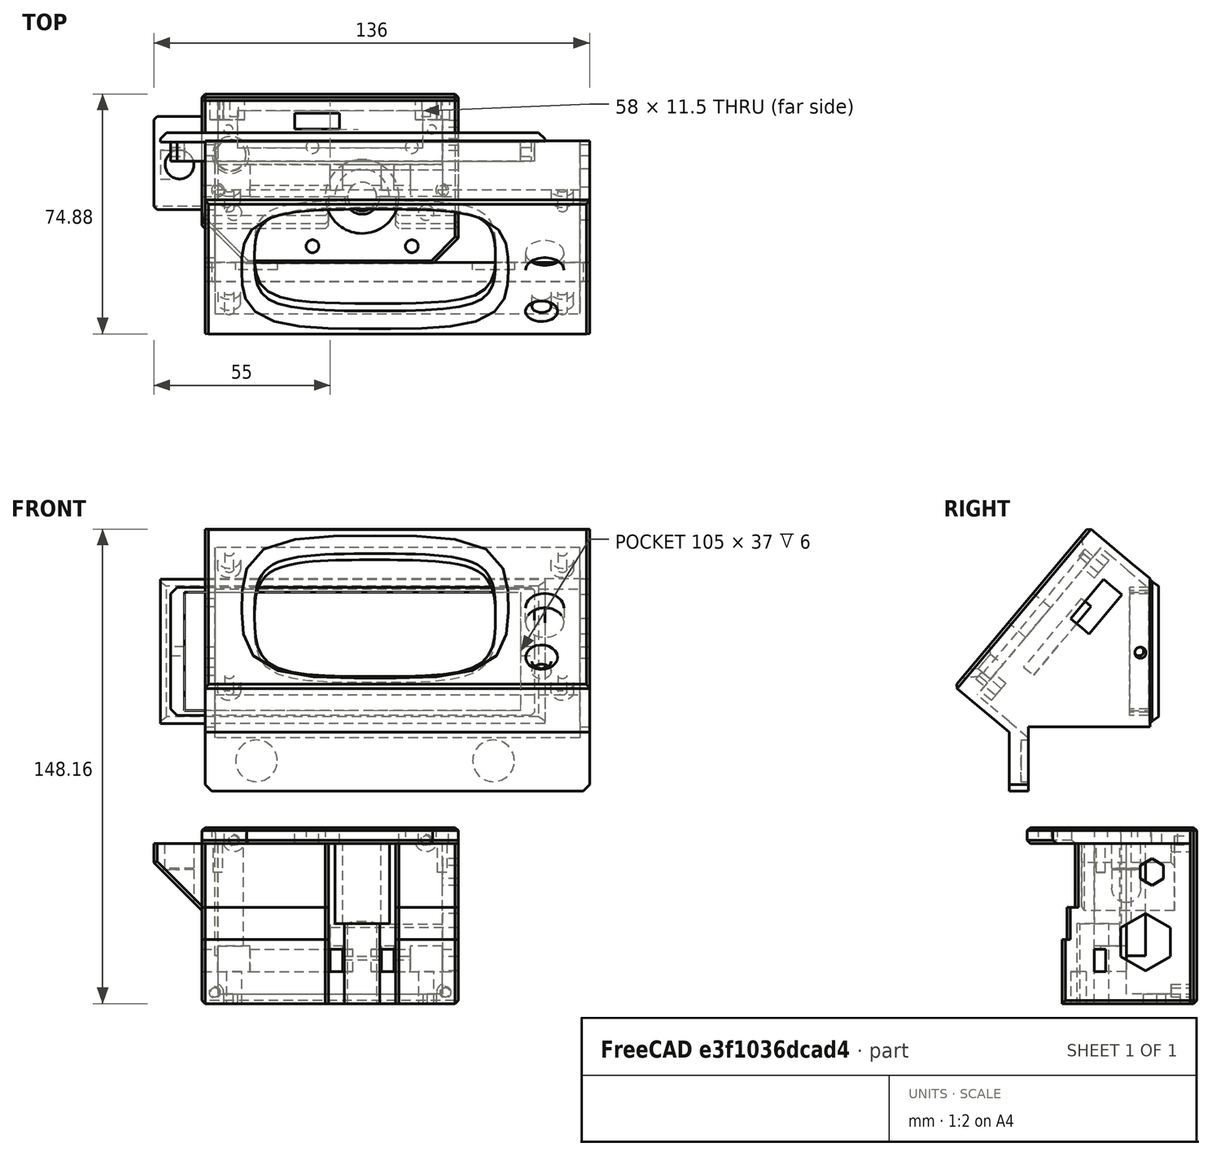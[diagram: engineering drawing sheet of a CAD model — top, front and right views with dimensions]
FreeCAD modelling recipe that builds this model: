
FCSTD DOCUMENT  (FreeCAD 0.19R)
Label: Ztower2
License: All rights reserved
LicenseURL: http://en.wikipedia.org/wiki/All_rights_reserved
objects: Sketcher::SketchObject×45, PartDesign::Pocket×31, PartDesign::Chamfer×18, PartDesign::Pad×13, PartDesign::Body×5, PartDesign::Mirrored×4, PartDesign::Fillet×1, Mesh::Feature×1
note: 180 computed .brp shape members not serialized (recipe doc carries the construction recipe); baked Part::Feature solids carry a one-line shape summary decoded from their .brp

FEATURE [Sketcher::SketchObject] Sketch  label="body"
  FullyConstrained = true
  MapMode = 5
  Support = -> [XY_Plane]
  sketch-geometry (6):
    g0: LineSegment StartX=-40 StartY=40 StartZ=0 EndX=40 EndY=40 EndZ=0
    g1: LineSegment StartX=40 StartY=40 StartZ=0 EndX=40 EndY=0 EndZ=0
    g2: LineSegment StartX=40 StartY=0 StartZ=0 EndX=-40 EndY=0 EndZ=0
    g3: LineSegment StartX=-40 StartY=0 StartZ=0 EndX=-40 EndY=40 EndZ=0
    g4: Circle CenterX=-30 CenterY=5 CenterZ=0 NormalX=0 NormalY=0 NormalZ=1 AngleXU=0 Radius=2.4
    g5: Circle CenterX=30 CenterY=5 CenterZ=0 NormalX=0 NormalY=0 NormalZ=1 AngleXU=0 Radius=2.4
  constraints (16):
    c: Coincident(g0,g1)
    c: Coincident(g1,g2)
    c: Coincident(g2,g3)
    c: Coincident(g3,g0)
    c: Horizontal(g0)
    c: Vertical(g1)
    c: Vertical(g3)
    c: PointOnObject(g1,g-1)
    c: Symmetric(g1,g2,g-2)
    c: Symmetric(g4,g5,g-2)
    c: Distance(g5,g4) = 60
    c: Diameter(g5) = 4.8
    c: Equal(g5,g4)
    c: DistanceY(g5) = 5
    c: Distance(g2) = 80
    c: Distance(g1) = 40
FEATURE [PartDesign::Pad] Pad
  Direction = (1,1,1)
  Length = 50
  Length2 = 100
  Profile = -> Sketch
  Type = 0
FEATURE [Sketcher::SketchObject] Sketch002  label="leadscrew"
  FullyConstrained = true
  MapMode = 5
  Placement = pos=(0,0,50) rot=(0,0,1;0rad)
  sketch-geometry (7):
    g0: Circle CenterX=10 CenterY=10 CenterZ=0 NormalX=0 NormalY=0 NormalZ=1 AngleXU=0 Radius=4.5
    g1: ArcOfCircle CenterX=10 CenterY=10 CenterZ=0 NormalX=0 NormalY=0 NormalZ=1 AngleXU=0 Radius=5.5 StartAngle=3.51376 EndAngle=5.91102
    g2: LineSegment StartX=4.87652 StartY=8 StartZ=0 EndX=0.876525 EndY=8 EndZ=0
    g3: LineSegment StartX=0.876525 StartY=8 StartZ=0 EndX=0.876525 EndY=-1.92 EndZ=0
    g4: LineSegment StartX=0.876525 StartY=-1.92 StartZ=0 EndX=19.1235 EndY=-1.92 EndZ=0
    g5: LineSegment StartX=19.1235 StartY=-1.92 StartZ=0 EndX=19.1235 EndY=8 EndZ=0
    g6: LineSegment StartX=15.1235 StartY=8 StartZ=0 EndX=19.1235 EndY=8 EndZ=0
  constraints (21):
    c: DistanceX(g0) = 10
    c: DistanceY(g0) = 10
    c: Diameter(g0) = 9
    c: Coincident(g1,g0)
    c: Coincident(g2,g1)
    c: Horizontal(g2)
    c: Coincident(g3,g2)
    c: Vertical(g3)
    c: Coincident(g4,g3)
    c: Horizontal(g4)
    c: Coincident(g5,g4)
    c: Vertical(g5)
    c: Coincident(g6,g1)
    c: Coincident(g6,g5)
    c: Horizontal(g6)
    c: DistanceY(g2) = 8
    c: DistanceY(g5) = 8
    c: Diameter(g1) = 11
    c: DistanceX(g2,g2) = 4
    c: Distance(g6) = 4
    c: DistanceY(g4) = -1.92
FEATURE [Sketcher::SketchObject] Sketch004  label="wiringbox"
  FullyConstrained = true
  MapMode = 5
  Placement = pos=(0,35,0) rot=(0,0.707107,0.707107;3.14159rad)
  sketch-geometry (4):
    g0: LineSegment StartX=-35 StartY=60 StartZ=0 EndX=35 EndY=60 EndZ=0
    g1: LineSegment StartX=35 StartY=60 StartZ=0 EndX=35 EndY=3 EndZ=0
    g2: LineSegment StartX=35 StartY=3 StartZ=0 EndX=-35 EndY=3 EndZ=0
    g3: LineSegment StartX=-35 StartY=3 StartZ=0 EndX=-35 EndY=60 EndZ=0
  constraints (11):
    c: Coincident(g0,g1)
    c: Coincident(g1,g2)
    c: Coincident(g2,g3)
    c: Coincident(g3,g0)
    c: Horizontal(g0)
    c: Vertical(g1)
    c: Vertical(g3)
    c: Symmetric(g1,g2,g-2)
    c: DistanceY(g1) = 3
    c: Distance(g2) = 70
    c: DistanceY(g0) = 60
FEATURE [Sketcher::SketchObject] Sketch005  label="DB37"
  FullyConstrained = false
  MapMode = 5
  Placement = pos=(0,1e-15,3) rot=(0,0,1;0rad)
  sketch-geometry (7):
    g0: LineSegment StartX=-29 StartY=36.75 StartZ=0 EndX=29 EndY=36.75 EndZ=0
    g1: LineSegment StartX=29 StartY=36.75 StartZ=0 EndX=29 EndY=25.25 EndZ=0
    g2: LineSegment StartX=29 StartY=25.25 StartZ=0 EndX=-29 EndY=25.25 EndZ=0
    g3: LineSegment StartX=-29 StartY=25.25 StartZ=0 EndX=-29 EndY=36.75 EndZ=0
    g4: Circle CenterX=-31.75 CenterY=31 CenterZ=0 NormalX=0 NormalY=0 NormalZ=1 AngleXU=0 Radius=1.4
    g5: Circle CenterX=31.75 CenterY=31 CenterZ=0 NormalX=0 NormalY=0 NormalZ=1 AngleXU=0 Radius=1.4
    g6: LineSegment StartX=-53.0593 StartY=31 StartZ=0 EndX=58.6364 EndY=31 EndZ=0
  constraints (17):
    c: Coincident(g0,g1)
    c: Coincident(g1,g2)
    c: Coincident(g2,g3)
    c: Coincident(g3,g0)
    c: Horizontal(g2)
    c: Vertical(g1)
    c: Vertical(g3)
    c: Distance(g0) = 58
    c: Symmetric(g0,g0,g-2)
    c: Distance(g1) = 11.5
    c: Distance(g5,g4) = 63.5
    c: Symmetric(g5,g4,g-2)
    c: Diameter(g5) = 2.8
    c: Equal(g5,g4)
    c: Symmetric(g2,g0,g6)
    c: PointOnObject(g4,g6)
    c: DistanceY(g6) = 31
FEATURE [Sketcher::SketchObject] Sketch006  label="sideports"
  FullyConstrained = true
  MapMode = 5
  Placement = pos=(-40,0,0) rot=(0.57735,-0.57735,-0.57735;2.0944rad)
  sketch-geometry (4):
    g0: LineSegment StartX=-13.5 StartY=17 StartZ=0 EndX=-10 EndY=17 EndZ=0
    g1: LineSegment StartX=-10 StartY=17 StartZ=0 EndX=-10 EndY=10 EndZ=0
    g2: LineSegment StartX=-10 StartY=10 StartZ=0 EndX=-13.5 EndY=10 EndZ=0
    g3: LineSegment StartX=-13.5 StartY=10 StartZ=0 EndX=-13.5 EndY=17 EndZ=0
  constraints (12):
    c: Coincident(g0,g1)
    c: Coincident(g1,g2)
    c: Coincident(g2,g3)
    c: Coincident(g3,g0)
    c: Horizontal(g0)
    c: Horizontal(g2)
    c: Vertical(g1)
    c: Vertical(g3)
    c: Distance(g2) = 3.5
    c: Distance(g3) = 7
    c: DistanceY(g1) = 10
    c: DistanceX(g1) = -10
FEATURE [Sketcher::SketchObject] Sketch007  label="ports"
  FullyConstrained = true
  MapMode = 5
  Placement = pos=(0,20,-5e-15) rot=(0,0.707107,0.707107;3.14159rad)
  sketch-geometry (8):
    g0: LineSegment StartX=-35 StartY=18 StartZ=0 EndX=-25 EndY=18 EndZ=0
    g1: LineSegment StartX=-25 StartY=18 StartZ=0 EndX=-25 EndY=10 EndZ=0
    g2: LineSegment StartX=-25 StartY=10 StartZ=0 EndX=-35 EndY=10 EndZ=0
    g3: LineSegment StartX=-35 StartY=10 StartZ=0 EndX=-35 EndY=18 EndZ=0
    g4: LineSegment StartX=25 StartY=18 StartZ=0 EndX=35 EndY=18 EndZ=0
    g5: LineSegment StartX=35 StartY=18 StartZ=0 EndX=35 EndY=10 EndZ=0
    g6: LineSegment StartX=35 StartY=10 StartZ=0 EndX=25 EndY=10 EndZ=0
    g7: LineSegment StartX=25 StartY=10 StartZ=0 EndX=25 EndY=18 EndZ=0
  constraints (23):
    c: Coincident(g0,g1)
    c: Coincident(g1,g2)
    c: Coincident(g2,g3)
    c: Coincident(g3,g0)
    c: Horizontal(g0)
    c: Horizontal(g2)
    c: Vertical(g1)
    c: Vertical(g3)
    c: Coincident(g4,g5)
    c: Coincident(g5,g6)
    c: Coincident(g6,g7)
    c: Coincident(g7,g4)
    c: Horizontal(g4)
    c: Horizontal(g6)
    c: Vertical(g5)
    c: Vertical(g7)
    c: DistanceY(g5) = 10
    c: DistanceY(g1) = 10
    c: Distance(g1) = 8
    c: Distance(g4) = 10
    c: Distance(g0) = 10
    c: Symmetric(g0,g4,g-2)
    c: DistanceX(g4) = 35
FEATURE [Sketcher::SketchObject] Sketch008  label="shtelfboss"
  FullyConstrained = true
  MapMode = 5
  Placement = pos=(0,35,0) rot=(0,0.707107,0.707107;3.14159rad)
  sketch-geometry (4):
    g0: LineSegment StartX=40 StartY=29 StartZ=0 EndX=55 EndY=44 EndZ=0
    g1: LineSegment StartX=55 StartY=44 StartZ=0 EndX=55 EndY=50 EndZ=0
    g2: LineSegment StartX=55 StartY=50 StartZ=0 EndX=40 EndY=50 EndZ=0
    g3: LineSegment StartX=40 StartY=50 StartZ=0 EndX=40 EndY=29 EndZ=0
  constraints (12):
    c: Coincident(g0,g1)
    c: Vertical(g1)
    c: Coincident(g1,g2)
    c: Horizontal(g2)
    c: Coincident(g2,g3)
    c: Coincident(g3,g0)
    c: Vertical(g3)
    c: DistanceX(g0) = 40
    c: Angle(g0) = 0.785398
    c: Distance(g1) = 6
    c: Distance(g2) = 15
    c: DistanceY(g2) = 50
FEATURE [Sketcher::SketchObject] Sketch009  label="umbillical"
  FullyConstrained = true
  MapMode = 5
  Placement = pos=(0,1.11e-14,50) rot=(0,0,1;0rad)
  sketch-geometry (8):
    g0: Circle CenterX=-47 CenterY=20 CenterZ=0 NormalX=0 NormalY=0 NormalZ=1 AngleXU=0 Radius=4.5
    g1: LineSegment StartX=-42.9 StartY=24.6329 StartZ=0 EndX=-42.9 EndY=29.3671 EndZ=0
    g2: LineSegment StartX=-42.9 StartY=29.3671 StartZ=0 EndX=-47 EndY=31.7343 EndZ=0
    g3: LineSegment StartX=-47 StartY=31.7343 StartZ=0 EndX=-51.1 EndY=29.3671 EndZ=0
    g4: LineSegment StartX=-51.1 StartY=29.3671 StartZ=0 EndX=-51.1 EndY=24.6329 EndZ=0
    g5: LineSegment StartX=-51.1 StartY=24.6329 StartZ=0 EndX=-47 EndY=22.2657 EndZ=0
    g6: LineSegment StartX=-47 StartY=22.2657 StartZ=0 EndX=-42.9 EndY=24.6329 EndZ=0
    g7: Circle CenterX=-47 CenterY=27 CenterZ=0 NormalX=0 NormalY=0 NormalZ=1 AngleXU=0 Radius=4.73427
  constraints (20):
    c: Diameter(g0) = 9
    c: DistanceX(g0) = -47
    c: Coincident(g1,g2)
    c: Coincident(g2,g3)
    c: Coincident(g3,g4)
    c: Coincident(g4,g5)
    c: Coincident(g5,g6)
    c: Coincident(g6,g1)
    c: Equal(g1, g2-g6) x5
    c: PointOnObject(g1,g7)
    c: PointOnObject(g2,g7)
    c: PointOnObject(g3,g7)
    c: PointOnObject(g4,g7)
    c: PointOnObject(g5,g7)
    c: PointOnObject(g6,g7)
    c: Distance(g4,g1) = 8.2
    c: DistanceX(g7) = -47
    c: Vertical(g4)
    c: DistanceY(g7) = 27
    c: DistanceY(g0) = 20
FEATURE [Sketcher::SketchObject] Sketch013  label="printhNotch"
  FullyConstrained = false
  MapMode = 5
  Placement = pos=(-52,0,0) rot=(0.57735,-0.57735,-0.57735;2.0944rad)
  sketch-geometry (4):
    g0: LineSegment StartX=-24.5 StartY=41.9 StartZ=0 EndX=-15.5 EndY=41.9 EndZ=0
    g1: LineSegment StartX=-15.5 StartY=41.9 StartZ=0 EndX=-15.5 EndY=36.1507 EndZ=0
    g2: LineSegment StartX=-15.5 StartY=36.1507 StartZ=0 EndX=-24.5 EndY=36.1507 EndZ=0
    g3: LineSegment StartX=-24.5 StartY=36.1507 StartZ=0 EndX=-24.5 EndY=41.9 EndZ=0
  constraints (11):
    c: Coincident(g0,g1)
    c: Coincident(g1,g2)
    c: Coincident(g2,g3)
    c: Coincident(g3,g0)
    c: Horizontal(g0)
    c: Horizontal(g2)
    c: Vertical(g1)
    c: Vertical(g3)
    c: Distance(g2) = 9
    c: DistanceX(g1) = -15.5
    c: DistanceY(g0) = 41.9
FEATURE [Sketcher::SketchObject] Sketch014  label="pritnfilm"
  FullyConstrained = false
  MapMode = 5
  Placement = pos=(0,0,41.9005) rot=(1,0,0;3.14159rad)
  sketch-geometry (4):
    g0: LineSegment StartX=-52.5605 StartY=-15.1127 StartZ=0 EndX=-40.6551 EndY=-15.1127 EndZ=0
    g1: LineSegment StartX=-40.6551 StartY=-15.1127 StartZ=0 EndX=-40.6551 EndY=-25.2911 EndZ=0
    g2: LineSegment StartX=-40.6551 StartY=-25.2911 StartZ=0 EndX=-52.5605 EndY=-25.2911 EndZ=0
    g3: LineSegment StartX=-52.5605 StartY=-25.2911 StartZ=0 EndX=-52.5605 EndY=-15.1127 EndZ=0
  constraints (8):
    c: Coincident(g0,g1)
    c: Coincident(g1,g2)
    c: Coincident(g2,g3)
    c: Coincident(g3,g0)
    c: Horizontal(g0)
    c: Horizontal(g2)
    c: Vertical(g1)
    c: Vertical(g3)
FEATURE [PartDesign::Pocket] Pocket
  BaseFeature = -> Pad
  Length = 5
  Length2 = 100
  Profile = -> Sketch002
  Type = 1
FEATURE [Sketcher::SketchObject] Sketch015  label="Coupler"
  FullyConstrained = true
  MapMode = 5
  Placement = pos=(0,0,50) rot=(0,0,1;0rad)
  Support = -> [Pocket]
  sketch-geometry (1):
    g0: Circle CenterX=10 CenterY=10 CenterZ=0 NormalX=0 NormalY=0 NormalZ=1 AngleXU=0 Radius=8.5
  constraints (3):
    c: DistanceX(g0) = 10
    c: DistanceY(g0) = 10
    c: Diameter(g0) = 17
FEATURE [PartDesign::Pocket] Pocket001
  BaseFeature = -> Pocket
  Length = 25
  Length2 = 100
  Profile = -> Sketch015
  Type = 0
FEATURE [PartDesign::Pocket] Pocket002
  BaseFeature = -> Pocket001
  Length = 15
  Length2 = 100
  Profile = -> Sketch004
  Type = 4
FEATURE [PartDesign::Pocket] Pocket003
  BaseFeature = -> Pocket002
  Length = 5
  Length2 = 100
  Profile = -> Sketch005
  Type = 0
FEATURE [PartDesign::Pocket] Pocket004
  BaseFeature = -> Pocket003
  Length = 5
  Length2 = 100
  Profile = -> Sketch006
  Type = 1
FEATURE [PartDesign::Pocket] Pocket005
  BaseFeature = -> Pocket004
  Length = 10
  Length2 = 100
  Profile = -> Sketch007
  Type = 0
FEATURE [PartDesign::Pad] Pad002
  BaseFeature = -> Pocket005
  Direction = (1,1,1)
  Length = 29
  Length2 = 100
  Profile = -> Sketch008
  Reversed = true
  Type = 0
FEATURE [PartDesign::Pocket] Pocket006
  BaseFeature = -> Pad002
  Length = 5
  Length2 = 100
  Profile = -> Sketch009
  Type = 1
FEATURE [PartDesign::Pocket] Pocket007
  BaseFeature = -> Pocket006
  Length = 5
  Length2 = 100
  Profile = -> Sketch013
  Type = 4
FEATURE [PartDesign::Pad] Pad003
  BaseFeature = -> Pocket007
  Direction = (1,1,1)
  Length = 0.3
  Length2 = 100
  Profile = -> Sketch014
  Reversed = true
  Type = 0
FEATURE [Sketcher::SketchObject] Sketch017  label="backReleif"
  FullyConstrained = true
  MapMode = 5
  Placement = pos=(40,0,0) rot=(0.57735,0.57735,0.57735;2.0944rad)
  sketch-geometry (6):
    g0: LineSegment StartX=4 StartY=53.2 StartZ=0 EndX=4 EndY=30 EndZ=0
    g1: LineSegment StartX=4 StartY=30 StartZ=0 EndX=1.5 EndY=30 EndZ=0
    g2: LineSegment StartX=-2.11 StartY=61.28 StartZ=0 EndX=4 EndY=53.2 EndZ=0
    g3: LineSegment StartX=1.5 StartY=30 StartZ=0 EndX=1.5 EndY=20 EndZ=0
    g4: LineSegment StartX=1.5 StartY=20 StartZ=0 EndX=-2.11 EndY=20 EndZ=0
    g5: LineSegment StartX=-2.11 StartY=20 StartZ=0 EndX=-2.11 EndY=61.28 EndZ=0
  constraints (18):
    c: Vertical(g0)
    c: Coincident(g0,g1)
    c: Coincident(g2,g0)
    c: DistanceX(g0) = 4
    c: DistanceY(g0) = 30
    c: Coincident(g1,g3)
    c: Vertical(g3)
    c: Coincident(g3,g4)
    c: Coincident(g4,g5)
    c: Vertical(g5)
    c: Coincident(g2,g5)
    c: Horizontal(g1)
    c: Horizontal(g4)
    c: DistanceY(g3) = 20
    c: DistanceX(g2) = -2.11
    c: DistanceY(g2) = 61.28
    c: DistanceY(g0) = 53.2
    c: DistanceX(g3) = 1.5
FEATURE [Sketcher::SketchObject] Sketch018  label="StepperPlatBolts"
  FullyConstrained = true
  MapMode = 5
  Placement = pos=(0,0,50) rot=(0,0,1;0rad)
  sketch-geometry (2):
    g0: Circle CenterX=-35 CenterY=12 CenterZ=0 NormalX=0 NormalY=0 NormalZ=1 AngleXU=0 Radius=1.4
    g1: Circle CenterX=35 CenterY=12 CenterZ=0 NormalX=0 NormalY=0 NormalZ=1 AngleXU=0 Radius=1.4
  constraints (5):
    c: Symmetric(g1,g0,g-2)
    c: Distance(g1,g0) = 70
    c: DistanceY(g1) = 12
    c: Diameter(g1) = 2.8
    c: Equal(g1,g0)
FEATURE [Sketcher::SketchObject] Sketch019  label="5mmbolts"
  FullyConstrained = true
  MapMode = 5
  Placement = pos=(0,0,0) rot=(1,0,0;3.14159rad)
  sketch-geometry (2):
    g0: Circle CenterX=-30 CenterY=-5 CenterZ=0 NormalX=0 NormalY=0 NormalZ=1 AngleXU=0 Radius=2.4
    g1: Circle CenterX=30 CenterY=-5 CenterZ=0 NormalX=0 NormalY=0 NormalZ=1 AngleXU=0 Radius=2.4
  constraints (5):
    c: Symmetric(g1,g0,g-2)
    c: Diameter(g1) = 4.8
    c: Equal(g1,g0)
    c: Distance(g1,g0) = 60
    c: DistanceY(g1) = -5
FEATURE [Sketcher::SketchObject] Sketch020  label="wirespace"
  FullyConstrained = true
  MapMode = 5
  Placement = pos=(0,0,0) rot=(1,0,0;3.14159rad)
  sketch-geometry (6):
    g0: ArcOfCircle CenterX=10 CenterY=-10 CenterZ=0 NormalX=0 NormalY=0 NormalZ=1 AngleXU=0 Radius=5.5 StartAngle=0 EndAngle=3.14159
    g1: LineSegment StartX=4.5 StartY=-10 StartZ=0 EndX=-0.5 EndY=-10 EndZ=0
    g2: LineSegment StartX=15.5 StartY=-10 StartZ=0 EndX=20.5 EndY=-10 EndZ=0
    g3: LineSegment StartX=20.5 StartY=-10 StartZ=0 EndX=20.5 EndY=2.44 EndZ=0
    g4: LineSegment StartX=-0.5 StartY=-10 StartZ=0 EndX=-0.5 EndY=2.44 EndZ=0
    g5: LineSegment StartX=-0.5 StartY=2.44 StartZ=0 EndX=20.5 EndY=2.44 EndZ=0
  constraints (19):
    c: Coincident(g1,g0)
    c: Horizontal(g1)
    c: Coincident(g2,g0)
    c: Horizontal(g2)
    c: Coincident(g3,g2)
    c: Vertical(g3)
    c: Coincident(g4,g1)
    c: Vertical(g4)
    c: Coincident(g5,g4)
    c: Coincident(g5,g3)
    c: Horizontal(g5)
    c: Distance(g2) = 5
    c: Distance(g1) = 5
    c: Diameter(g0) = 11
    c: DistanceY(g0) = -10
    c: DistanceY(g0) = -10
    c: DistanceX(g0) = 10
    c: DistanceY(g0) = -10
    c: DistanceY(g4) = 2.44
FEATURE [Sketcher::SketchObject] Sketch021  label="wirports"
  FullyConstrained = true
  MapMode = 5
  Placement = pos=(0,12,0) rot=(1,0,0;1.5708rad)
  sketch-geometry (8):
    g0: LineSegment StartX=16 StartY=18 StartZ=0 EndX=20 EndY=18 EndZ=0
    g1: LineSegment StartX=20 StartY=18 StartZ=0 EndX=20 EndY=10 EndZ=0
    g2: LineSegment StartX=20 StartY=10 StartZ=0 EndX=16 EndY=10 EndZ=0
    g3: LineSegment StartX=16 StartY=10 StartZ=0 EndX=16 EndY=18 EndZ=0
    g4: LineSegment StartX=0 StartY=18 StartZ=0 EndX=4 EndY=18 EndZ=0
    g5: LineSegment StartX=4 StartY=18 StartZ=0 EndX=4 EndY=10 EndZ=0
    g6: LineSegment StartX=4 StartY=10 StartZ=0 EndX=0 EndY=10 EndZ=0
    g7: LineSegment StartX=0 StartY=10 StartZ=0 EndX=0 EndY=18 EndZ=0
  constraints (24):
    c: Coincident(g0,g1)
    c: Coincident(g1,g2)
    c: Coincident(g2,g3)
    c: Coincident(g3,g0)
    c: Horizontal(g0)
    c: Horizontal(g2)
    c: Vertical(g1)
    c: Vertical(g3)
    c: Coincident(g4,g5)
    c: Coincident(g5,g6)
    c: Coincident(g6,g7)
    c: Coincident(g7,g4)
    c: Horizontal(g4)
    c: Horizontal(g6)
    c: Vertical(g5)
    c: Vertical(g7)
    c: PointOnObject(g4,g-2)
    c: DistanceY(g5) = 10
    c: DistanceY(g2) = 10
    c: DistanceY(g0) = 18
    c: DistanceY(g4) = 18
    c: DistanceX(g2) = 16
    c: DistanceX(g5) = 4
    c: DistanceX(g1) = 20
FEATURE [Sketcher::SketchObject] Sketch026  label="thickenerbump"
  FullyConstrained = false
  MapMode = 5
  Placement = pos=(0,0,50) rot=(0,0,1;0rad)
  sketch-geometry (4):
    g0: ArcOfCircle CenterX=9.88904 CenterY=9.80854 CenterZ=0 NormalX=0 NormalY=0 NormalZ=1 AngleXU=0 Radius=11.7902 StartAngle=0.279522 EndAngle=2.4698
    g1: ArcOfCircle CenterX=9.88904 CenterY=9.80854 CenterZ=0 NormalX=0 NormalY=0 NormalZ=1 AngleXU=0 Radius=9.47005 StartAngle=0.269167 EndAngle=2.60322
    g2: LineSegment StartX=1.75858 StartY=14.6642 StartZ=0 EndX=0.660759 EndY=17.1467 EndZ=0
    g3: LineSegment StartX=19.0181 StartY=12.3269 StartZ=0 EndX=21.2217 EndY=13.0614 EndZ=0
  constraints (5):
    c: Coincident(g1,g0)
    c: Coincident(g2,g1)
    c: Coincident(g2,g0)
    c: Coincident(g3,g1)
    c: Coincident(g3,g0)
FEATURE [Sketcher::SketchObject] Sketch003
  FullyConstrained = false
  MapMode = 5
  Support = -> [XY_Plane001]
  sketch-geometry (24):
    g0: LineSegment StartX=-11 StartY=31 StartZ=0 EndX=31 EndY=31 EndZ=0
    g1: LineSegment StartX=31 StartY=31 StartZ=0 EndX=31 EndY=-11 EndZ=0
    g2: LineSegment StartX=31 StartY=-11 StartZ=0 EndX=-11 EndY=-11 EndZ=0
    g3: LineSegment StartX=-11 StartY=-11 StartZ=0 EndX=-11 EndY=31 EndZ=0
    g4: Circle CenterX=10 CenterY=10 CenterZ=0 NormalX=0 NormalY=0 NormalZ=1 AngleXU=0 Radius=0.980681
    g5: LineSegment StartX=-40 StartY=40 StartZ=0 EndX=40 EndY=40 EndZ=0
    g6: LineSegment StartX=40 StartY=40 StartZ=0 EndX=40 EndY=-3 EndZ=0
    g7: LineSegment StartX=32 StartY=-11 StartZ=0 EndX=-26 EndY=-11 EndZ=0
    g8: LineSegment StartX=-40 StartY=3 StartZ=0 EndX=-40 EndY=40 EndZ=0
    g9: LineSegment StartX=-43.1827 StartY=10 StartZ=0 EndX=48.034 EndY=10 EndZ=0
    g10: Circle CenterX=10 CenterY=10 CenterZ=0 NormalX=0 NormalY=0 NormalZ=1 AngleXU=0 Radius=11.5
    g11: Circle CenterX=-35 CenterY=12 CenterZ=0 NormalX=0 NormalY=0 NormalZ=1 AngleXU=0 Radius=2
    g12: Circle CenterX=35 CenterY=12 CenterZ=0 NormalX=0 NormalY=0 NormalZ=1 AngleXU=0 Radius=2
    g13: LineSegment StartX=-11.0178 StartY=36.0399 StartZ=0 EndX=2.98222 EndY=36.0399 EndZ=0
    g14: LineSegment StartX=2.98222 StartY=36.0399 StartZ=0 EndX=2.98222 EndY=31.0399 EndZ=0
    g15: LineSegment StartX=2.98222 StartY=31.0399 StartZ=0 EndX=-11.0178 EndY=31.0399 EndZ=0
    g16: LineSegment StartX=-11.0178 StartY=31.0399 StartZ=0 EndX=-11.0178 EndY=36.0399 EndZ=0
    g17: Circle CenterX=25.5 CenterY=-5.5 CenterZ=0 NormalX=0 NormalY=0 NormalZ=1 AngleXU=0 Radius=2
    g18: Circle CenterX=-5.5 CenterY=25.5 CenterZ=0 NormalX=0 NormalY=0 NormalZ=1 AngleXU=0 Radius=2
    g19: Circle CenterX=-31 CenterY=23 CenterZ=0 NormalX=0 NormalY=0 NormalZ=1 AngleXU=0 Radius=4.75
    g20: Circle CenterX=25.5 CenterY=25.5 CenterZ=0 NormalX=0 NormalY=0 NormalZ=1 AngleXU=0 Radius=2
    g21: Circle CenterX=-5.5 CenterY=-5.5 CenterZ=0 NormalX=0 NormalY=0 NormalZ=1 AngleXU=0 Radius=2
    g22: LineSegment StartX=-40 StartY=3 StartZ=0 EndX=-26 EndY=-11 EndZ=0
    g23: LineSegment StartX=40 StartY=-3 StartZ=0 EndX=32 EndY=-11 EndZ=0
  constraints (62):
    c: Coincident(g0,g1)
    c: Coincident(g1,g2)
    c: Coincident(g2,g3)
    c: Coincident(g3,g0)
    c: Horizontal(g0)
    c: Horizontal(g2)
    c: Vertical(g1)
    c: Vertical(g3)
    c: Distance(g1) = 42
    c: Distance(g0) = 42
    c: Symmetric(g2,g0,g4)
    c: DistanceY(g4) = 10
    c: DistanceX(g4) = 10
    c: Coincident(g5,g6)
    c: Coincident(g8,g5)
    c: Horizontal(g5)
    c: Vertical(g6)
    c: Vertical(g8)
    c: DistanceY(g9) = 10
    c: Coincident(g10,g4)
    c: Diameter(g10) = 23
    c: DistanceY(g5) = 40
    c: Symmetric(g12,g11,g-2)
    c: Distance(g11,g12) = 70
    c: Diameter(g11) = 4
    c: Diameter(g12) = 4
    c: DistanceY(g12) = 12
    c: Coincident(g13,g14)
    c: Coincident(g14,g15)
    c: Coincident(g15,g16)
    c: Coincident(g16,g13)
    c: Horizontal(g13)
    c: Horizontal(g15)
    c: Vertical(g14)
    c: Vertical(g16)
    c: DistanceY(g10,g18) = 15.5
    c: DistanceX(g18,g10) = 15.5
    c: Diameter(g18) = 4
    c: Symmetric(g17,g18,g10)
    c: Diameter(g17) = 4
    c: Distance(g13) = 14
    c: Distance(g16) = 5
    c: DistanceX(g19) = -31
    c: DistanceY(g19) = 23
    c: Diameter(g19) = 9.5
    c: Symmetric(g20,g21,g10)
    c: Diameter(g20) = 4
    c: Equal(g20,g21)
    c: DistanceX(g10,g20) = 15.5
    c: DistanceY(g10,g20) = 15.5
    c: DistanceY(g8) = 3
    c: DistanceX(g5) = -40
    c: Coincident(g22,g8)
    c: Coincident(g7,g22)
    c: Angle(g22) = -0.785398
    c: DistanceX(g6) = 40
    c: Coincident(g23,g6)
    c: Coincident(g23,g7)
    c: Angle(g23) = -2.35619
    c: Horizontal(g7)
    c: DistanceY(g7) = -11
    c: DistanceY(g6) = -3
FEATURE [PartDesign::Pad] Pad001
  Direction = (1,1,1)
  Length = 5
  Length2 = 100
  Profile = -> Sketch003
  Type = 0
FEATURE [Sketcher::SketchObject] Sketch027
  FullyConstrained = true
  MapMode = 5
  Placement = pos=(0,0,13.5) rot=(1,0,0;3.14159rad)
  sketch-geometry (4):
    g0: LineSegment StartX=-50 StartY=30 StartZ=0 EndX=64 EndY=30 EndZ=0
    g1: LineSegment StartX=64 StartY=30 StartZ=0 EndX=64 EndY=-30 EndZ=0
    g2: LineSegment StartX=64 StartY=-30 StartZ=0 EndX=-50 EndY=-30 EndZ=0
    g3: LineSegment StartX=-50 StartY=-30 StartZ=0 EndX=-50 EndY=30 EndZ=0
  constraints (11):
    c: Coincident(g0,g1)
    c: Coincident(g1,g2)
    c: Coincident(g2,g3)
    c: Coincident(g3,g0)
    c: Horizontal(g0)
    c: Horizontal(g2)
    c: Vertical(g1)
    c: DistanceX(g0) = 64
    c: DistanceX(g0) = -50
    c: Distance(g3) = 60
    c: Symmetric(g2,g0,g-1)
FEATURE [Sketcher::SketchObject] Sketch028  label="knob"
  FullyConstrained = false
  MapMode = 5
  Placement = pos=(0,0,0) rot=(1,0,0;3.14159rad)
  sketch-geometry (1):
    g0: Circle CenterX=52 CenterY=20.5 CenterZ=0 NormalX=0 NormalY=0 NormalZ=1 AngleXU=0 Radius=3
  constraints (1):
    c: Diameter(g0) = 6
FEATURE [Sketcher::SketchObject] Sketch029
  FullyConstrained = true
  MapMode = 5
  Support = -> [XY_Plane002]
  sketch-geometry (30):
    g0: LineSegment StartX=-53 StartY=32.5 StartZ=0 EndX=67 EndY=32.5 EndZ=0
    g1: LineSegment StartX=67 StartY=32.5 StartZ=0 EndX=67 EndY=-32.5 EndZ=0
    g2: LineSegment StartX=67 StartY=-32.5 StartZ=0 EndX=-53 EndY=-32.5 EndZ=0
    g3: LineSegment StartX=-53 StartY=-32.5 StartZ=0 EndX=-53 EndY=32.5 EndZ=0
    g4: LineSegment StartX=-37 StartY=24.5 StartZ=0 EndX=37 EndY=24.5 EndZ=0
    g5: LineSegment StartX=37 StartY=24.5 StartZ=0 EndX=37 EndY=-24.5 EndZ=0
    g6: LineSegment StartX=37 StartY=-24.5 StartZ=0 EndX=-37 EndY=-24.5 EndZ=0
    g7: LineSegment StartX=-37 StartY=-24.5 StartZ=0 EndX=-37 EndY=24.5 EndZ=0
    g8: LineSegment StartX=-37.7408 StartY=25.116 StartZ=0 EndX=37.7408 EndY=25.116 EndZ=0
    g9: LineSegment StartX=37.7408 StartY=25.116 StartZ=0 EndX=37.7408 EndY=-25.116 EndZ=0
    g10: LineSegment StartX=37.7408 StartY=-25.116 StartZ=0 EndX=-37.7408 EndY=-25.116 EndZ=0
    g11: LineSegment StartX=-37.7408 StartY=-25.116 StartZ=0 EndX=-37.7408 EndY=25.116 EndZ=0
    g12-g19: Circle x8 (B-spline internal-alignment scaffolding for g20; pole/knot coordinates omitted)
    g20: BSplineCurve PolesCount=8 KnotsCount=9 Degree=3 IsPeriodic=1
    g21-g29: GeomPoint x9 (B-spline internal-alignment scaffolding for g20; pole/knot coordinates omitted)
  constraints (53):
    c: Coincident(g0,g1)
    c: Coincident(g1,g2)
    c: Coincident(g2,g3)
    c: Coincident(g3,g0)
    c: Horizontal(g0)
    c: Horizontal(g2)
    c: Vertical(g1)
    c: Vertical(g3)
    c: Coincident(g4,g5)
    c: Coincident(g5,g6)
    c: Coincident(g6,g7)
    c: Coincident(g7,g4)
    c: Horizontal(g4)
    c: Vertical(g7)
    c: Distance(g5) = 49
    c: Distance(g4,g3) = 16
    c: Distance(g0,g5) = 30
    c: Distance(g6,g2) = 8
    c: Distance(g4,g0) = 8
    c: Distance(g6) = 74
    c: Symmetric(g5,g6,g-2)
    c: Symmetric(g5,g4,g-1)
    c: Coincident(g8,g9)
    c: Coincident(g9,g10)
    c: Coincident(g10,g11)
    c: Coincident(g11,g8)
    c: Horizontal(g8)
    c: Horizontal(g10)
    c: Vertical(g9)
    c: Vertical(g11)
    c: Symmetric(g9,g8,g-1)
    c: Weight(g12) = 1
    c: Equal(g12,g13)
    c: Equal(g12,g14)
    c: Equal(g12,g15)
    c: PointOnObject(g15,g-1)
    c: Equal(g12,g16)
    c: Equal(g12,g17)
    c: PointOnObject(g17,g-2)
    c: Equal(g12,g18)
    c: Equal(g12,g19)
    c: InternalAlignment(g12-g19 -> g20) x8
    c: InternalAlignment(g21-g29 -> g20) x9
    c: Coincident(g8,g12)
    c: Coincident(g14,g8)
    c: Coincident(g16,g10)
    c: Coincident(g18,g9)
    c: Distance(g19,g5) = 0.5
    c: Symmetric(g19,g15,g-2)
    c: Distance(g17,g6) = 0.5
    c: Symmetric(g17,g13,g-1)
    c: DistanceX(g8) = 37.7408
    c: DistanceY(g8) = 25.116
FEATURE [PartDesign::Pad] Pad005
  Direction = (1,1,1)
  Length = 25
  Length2 = 100
  Profile = -> Sketch029
  Type = 0
FEATURE [PartDesign::Pocket] Pocket016
  BaseFeature = -> Pad005
  Length = 5
  Length2 = 100
  Profile = -> Sketch028
  Type = 1
FEATURE [Sketcher::SketchObject] Sketch001  label="knob001"
  FullyConstrained = false
  MapMode = 5
  Placement = pos=(0,0,25) rot=(0,0,1;0rad)
  Support = -> [Pocket016]
  sketch-geometry (1):
    g0: Circle CenterX=53 CenterY=-0.5 CenterZ=0 NormalX=0 NormalY=0 NormalZ=1 AngleXU=0 Radius=6
  constraints (2):
    c: Diameter(g0) = 12
    c: DistanceY(g0) = -0.5
FEATURE [PartDesign::Pocket] Pocket017
  BaseFeature = -> Pocket016
  Length = 5
  Length2 = 100
  Profile = -> Sketch001
  Type = 1
FEATURE [Sketcher::SketchObject] Sketch030
  FullyConstrained = true
  MapMode = 5
  Placement = pos=(0,0,0) rot=(1,0,0;3.14159rad)
  Support = -> [Pocket017]
  sketch-geometry (4):
    g0: LineSegment StartX=-50 StartY=30 StartZ=0 EndX=64 EndY=30 EndZ=0
    g1: LineSegment StartX=64 StartY=30 StartZ=0 EndX=64 EndY=-30 EndZ=0
    g2: LineSegment StartX=64 StartY=-30 StartZ=0 EndX=-50 EndY=-30 EndZ=0
    g3: LineSegment StartX=-50 StartY=-30 StartZ=0 EndX=-50 EndY=30 EndZ=0
  constraints (11):
    c: Coincident(g0,g1)
    c: Coincident(g1,g2)
    c: Coincident(g2,g3)
    c: Coincident(g3,g0)
    c: Horizontal(g0)
    c: Horizontal(g2)
    c: Vertical(g1)
    c: Symmetric(g2,g0,g-1)
    c: DistanceX(g0) = -50
    c: DistanceY(g0) = 30
    c: DistanceX(g1) = 64
FEATURE [PartDesign::Pocket] Pocket018
  BaseFeature = -> Pocket017
  Length = 18
  Length2 = 100
  Profile = -> Sketch030
  Type = 0
FEATURE [PartDesign::Chamfer] Chamfer001
  Angle = 45
  Base = -> Pocket018 [Edge19]
  BaseFeature = -> Pocket018
  ChamferType = 0
  FlipDirection = false
  Size = 4
  Size2 = 1
  SupportTransform = false
FEATURE [Sketcher::SketchObject] Sketch031  label="standofs"
  FullyConstrained = true
  MapMode = 5
  Placement = pos=(0,0,18) rot=(1,0,0;3.14159rad)
  Support = -> [Chamfer001]
  sketch-geometry (4):
    g0: Circle CenterX=-45.5 CenterY=25 CenterZ=0 NormalX=0 NormalY=0 NormalZ=1 AngleXU=0 Radius=3.5
    g1: Circle CenterX=-45.5 CenterY=-25 CenterZ=0 NormalX=0 NormalY=0 NormalZ=1 AngleXU=0 Radius=3.5
    g2: Circle CenterX=58.5 CenterY=-25 CenterZ=0 NormalX=0 NormalY=0 NormalZ=1 AngleXU=0 Radius=3.5
    g3: Circle CenterX=58.5 CenterY=25 CenterZ=0 NormalX=0 NormalY=0 NormalZ=1 AngleXU=0 Radius=3.5
  constraints (10):
    c: Diameter(g0) = 7
    c: Equal(g0,g1)
    c: Equal(g0,g3)
    c: Equal(g0,g2)
    c: Symmetric(g1,g0,g-1)
    c: Symmetric(g2,g3,g-1)
    c: Distance(g3,g2) = 50
    c: Distance(g1,g0) = 50
    c: Distance(g3,g0) = 104
    c: DistanceX(g0) = -45.5
FEATURE [PartDesign::Pad] Pad006
  BaseFeature = -> Chamfer001
  Direction = (1,1,1)
  Length = 4.5
  Length2 = 100
  Profile = -> Sketch031
  Type = 0
FEATURE [Sketcher::SketchObject] Sketch032  label="holes"
  FullyConstrained = true
  MapMode = 5
  Placement = pos=(0,0,13.5) rot=(1,0,0;3.14159rad)
  Support = -> [Pad006]
  sketch-geometry (4):
    g0: Circle CenterX=-45.5 CenterY=25 CenterZ=0 NormalX=0 NormalY=0 NormalZ=1 AngleXU=0 Radius=1.4
    g1: Circle CenterX=58.5 CenterY=25 CenterZ=0 NormalX=0 NormalY=0 NormalZ=1 AngleXU=0 Radius=1.4
    g2: Circle CenterX=58.5 CenterY=-25 CenterZ=0 NormalX=0 NormalY=0 NormalZ=1 AngleXU=0 Radius=1.4
    g3: Circle CenterX=-45.5 CenterY=-25 CenterZ=0 NormalX=0 NormalY=0 NormalZ=1 AngleXU=0 Radius=1.4
  constraints (10):
    c: Distance(g3,g2) = 104
    c: Distance(g3,g0) = 50
    c: Symmetric(g3,g0,g-1)
    c: Symmetric(g2,g1,g-1)
    c: Diameter(g1) = 2.8
    c: Equal(g1,g2)
    c: Equal(g1,g3)
    c: Equal(g1,g0)
    c: DistanceX(g0) = -45.5
    c: Distance(g1,g2) = 50
FEATURE [PartDesign::Pocket] Pocket019
  BaseFeature = -> Pad006
  Length = 8
  Length2 = 100
  Profile = -> Sketch032
  Type = 0
FEATURE [Sketcher::SketchObject] Sketch033
  ExternalGeometry = -> [Pocket019]
  FullyConstrained = true
  MapMode = 5
  Placement = pos=(67,0,0) rot=(0.57735,0.57735,0.57735;2.0944rad)
  Support = -> [Pocket019]
  sketch-geometry (4):
    g0: LineSegment StartX=7 StartY=6.5 StartZ=0 EndX=23 EndY=6.5 EndZ=0
    g1: LineSegment StartX=23 StartY=6.5 StartZ=0 EndX=23 EndY=0 EndZ=0
    g2: LineSegment StartX=23 StartY=0 StartZ=0 EndX=7 EndY=0 EndZ=0
    g3: LineSegment StartX=7 StartY=0 StartZ=0 EndX=7 EndY=6.5 EndZ=0
  constraints (12):
    c: Coincident(g0,g1)
    c: Coincident(g1,g2)
    c: Coincident(g2,g3)
    c: Coincident(g3,g0)
    c: Horizontal(g0)
    c: Horizontal(g2)
    c: Vertical(g1)
    c: Vertical(g3)
    c: Distance(g-3,g0) = 7
    c: Distance(g0) = 16
    c: Distance(g0,g-4) = 7
    c: PointOnObject(g1,g-1)
FEATURE [PartDesign::Pocket] Pocket020
  BaseFeature = -> Pocket019
  Length = 9
  Length2 = 100
  Profile = -> Sketch033
  Type = 0
FEATURE [Sketcher::SketchObject] Sketch034
  ExternalGeometry = -> [Pocket020]
  FullyConstrained = true
  MapMode = 5
  Placement = pos=(-53,0,0) rot=(0.57735,-0.57735,-0.57735;2.0944rad)
  Support = -> [Pocket020]
  sketch-geometry (4):
    g0: LineSegment StartX=-14 StartY=12.5 StartZ=0 EndX=14 EndY=12.5 EndZ=0
    g1: LineSegment StartX=14 StartY=12.5 StartZ=0 EndX=14 EndY=8.5 EndZ=0
    g2: LineSegment StartX=14 StartY=8.5 StartZ=0 EndX=-14 EndY=8.5 EndZ=0
    g3: LineSegment StartX=-14 StartY=8.5 StartZ=0 EndX=-14 EndY=12.5 EndZ=0
  constraints (11):
    c: Coincident(g0,g1)
    c: Coincident(g1,g2)
    c: Coincident(g2,g3)
    c: Coincident(g3,g0)
    c: Horizontal(g0)
    c: Vertical(g1)
    c: Vertical(g3)
    c: Distance(g0,g-3) = 1
    c: Distance(g1) = 4
    c: Symmetric(g1,g2,g-2)
    c: Distance(g2) = 28
FEATURE [PartDesign::Pocket] Pocket021
  BaseFeature = -> Pocket020
  Length = 5
  Length2 = 100
  Profile = -> Sketch034
  Type = 0
FEATURE [Sketcher::SketchObject] Sketch010
  FullyConstrained = false
  MapMode = 5
  Placement = pos=(-53,0,0) rot=(0.57735,-0.57735,-0.57735;2.0944rad)
  Support = -> [Pocket021]
  sketch-geometry (8):
    g0: LineSegment StartX=2.97644 StartY=-29.7683 StartZ=0 EndX=27.4024 EndY=-0.658582 EndZ=0
    g1: LineSegment StartX=27.4024 StartY=-0.658582 StartZ=0 EndX=42.7233 EndY=-13.5143 EndZ=0
    g2: LineSegment StartX=42.7233 StartY=-13.5143 StartZ=0 EndX=46.58 EndY=-8.91807 EndZ=0
    g3: LineSegment StartX=46.58 StartY=-8.91807 StartZ=0 EndX=27.4809 EndY=7.10801 EndZ=0
    g4: LineSegment StartX=-32.5 StartY=0 StartZ=0 EndX=2.97644 EndY=-29.7683 EndZ=0
    g5: LineSegment StartX=2.97644 StartY=-29.7683 StartZ=0 EndX=-60.5281 EndY=23.5183 EndZ=0
    g6: LineSegment StartX=27.4809 StartY=7.10801 StartZ=0 EndX=-32.5 EndY=7.10801 EndZ=0
    g7: LineSegment StartX=-32.5 StartY=7.10801 StartZ=0 EndX=-32.5 EndY=0 EndZ=0
  constraints (21):
    c: Coincident(g0,g1)
    c: Perpendicular(g1,g0)
    c: Coincident(g1,g2)
    c: Coincident(g2,g3)
    c: Coincident(g4,g0)
    c: Distance(g0) = 38
    c: Parallel(g1,g3)
    c: Perpendicular(g0,g4)
    c: Perpendicular(g1,g2)
    c: Distance(g2) = 6
    c: Angle(g0) = 0.872665
    c: Coincident(g5,g0)
    c: Perpendicular(g0,g5)
    c: PointOnObject(g4,g-1)
    c: Distance(g1) = 20
    c: Coincident(g6,g3)
    c: Horizontal(g6)
    c: DistanceX(g6) = -32.5
    c: Coincident(g7,g6)
    c: Vertical(g7)
    c: Coincident(g4,g7)
FEATURE [PartDesign::Pad] Pad007
  BaseFeature = -> Pocket021
  Direction = (1,1,1)
  Length = 120
  Length2 = 100
  Profile = -> Sketch010
  Reversed = true
  Type = 0
FEATURE [PartDesign::Pocket] Pocket022
  BaseFeature = -> Pad007
  Length = 47
  Length2 = 100
  Profile = -> Sketch027
  Reversed = true
  Type = 0
FEATURE [Sketcher::SketchObject] Sketch016
  FullyConstrained = true
  MapMode = 5
  Placement = pos=(67,0,0) rot=(0.57735,0.57735,0.57735;2.0944rad)
  Support = -> [Pocket022]
  sketch-geometry (4):
    g0: LineSegment StartX=7 StartY=11 StartZ=0 EndX=23 EndY=11 EndZ=0
    g1: LineSegment StartX=23 StartY=11 StartZ=0 EndX=23 EndY=3.5 EndZ=0
    g2: LineSegment StartX=23 StartY=3.5 StartZ=0 EndX=7 EndY=3.5 EndZ=0
    g3: LineSegment StartX=7 StartY=3.5 StartZ=0 EndX=7 EndY=11 EndZ=0
  constraints (12):
    c: Coincident(g0,g1)
    c: Coincident(g1,g2)
    c: Coincident(g2,g3)
    c: Coincident(g3,g0)
    c: Horizontal(g0)
    c: Horizontal(g2)
    c: Vertical(g1)
    c: Vertical(g3)
    c: Distance(g1) = 7.5
    c: Distance(g2) = 16
    c: DistanceX(g0) = 7
    c: DistanceY(g0) = 11
FEATURE [PartDesign::Pocket] Pocket023
  BaseFeature = -> Pocket022
  Length = 9
  Length2 = 100
  Profile = -> Sketch016
  Type = 0
FEATURE [PartDesign::Chamfer] Chamfer002
  Angle = 45
  Base = -> Pocket023 [Edge6]
  BaseFeature = -> Pocket023
  ChamferType = 0
  FlipDirection = false
  Size = 2
  Size2 = 1
  SupportTransform = false
FEATURE [Sketcher::SketchObject] Sketch022
  ExternalGeometry = -> [Chamfer002]
  FullyConstrained = true
  MapMode = 5
  Placement = pos=(-53,0,0) rot=(0.57735,-0.57735,-0.57735;2.0944rad)
  Support = -> [Chamfer002]
  sketch-geometry (2):
    g0: Circle CenterX=-12.8334 CenterY=-12.586 CenterZ=0 NormalX=0 NormalY=0 NormalZ=1 AngleXU=0 Radius=1.75
    g1: LineSegment StartX=-30.5716 StartY=2.29813 StartZ=0 EndX=4.90481 EndY=-27.4701 EndZ=0
  constraints (6):
    c: Parallel(g1,g-3)
    c: Distance(g1,g-3) = 3
    c: Equal(g1,g-3)
    c: Symmetric(g1,g1,g0)
    c: Diameter(g0) = 3.5
    c: PointOnObject(g1,g-4)
FEATURE [PartDesign::Pocket] Pocket024
  BaseFeature = -> Chamfer002
  Length = 5
  Length2 = 100
  Profile = -> Sketch022
  Type = 1
FEATURE [PartDesign::Chamfer] Chamfer005
  Angle = 45
  Base = -> Pocket024 [Edge97]
  BaseFeature = -> Pocket024
  ChamferType = 0
  FlipDirection = false
  Size = 2
  Size2 = 1
  SupportTransform = false
FEATURE [PartDesign::Chamfer] Chamfer006
  Angle = 45
  Base = -> Chamfer005 [Edge23]
  BaseFeature = -> Chamfer005
  ChamferType = 0
  FlipDirection = false
  Size = 2
  Size2 = 1
  SupportTransform = false
FEATURE [Sketcher::SketchObject] Sketch023
  FullyConstrained = true
  MapMode = 5
  Placement = pos=(0,-10.9977,13.1066) rot=(1,0,0;3.83972rad)
  Support = -> [Chamfer006]
  sketch-geometry (2):
    g0: Circle CenterX=-37 CenterY=32 CenterZ=0 NormalX=0 NormalY=0 NormalZ=1 AngleXU=0 Radius=6.5
    g1: Circle CenterX=37 CenterY=32 CenterZ=0 NormalX=0 NormalY=0 NormalZ=1 AngleXU=0 Radius=6.5
  constraints (5):
    c: Diameter(g1) = 13
    c: Equal(g1,g0)
    c: Symmetric(g1,g0,g-2)
    c: DistanceY(g0) = 32
    c: Distance(g1,g0) = 74
FEATURE [PartDesign::Pocket] Pocket025
  BaseFeature = -> Chamfer006
  Length = 2.3
  Length2 = 100
  Profile = -> Sketch023
  Type = 0
FEATURE [PartDesign::Chamfer] Chamfer007
  Angle = 45
  Base = -> Pocket025 [Edge74,Edge75,Edge31,Edge67]
  BaseFeature = -> Pocket025
  ChamferType = 0
  FlipDirection = false
  Size = 1
  Size2 = 1
  SupportTransform = false
FEATURE [Sketcher::SketchObject] Sketch035
  ExternalGeometry = -> [Chamfer002]
  FullyConstrained = false
  MapMode = 5
  Placement = pos=(0,13.4282,-16.0031) rot=(1,0,0;3.83972rad)
  Support = -> [Chamfer002]
  sketch-geometry (4):
    g0: LineSegment StartX=-53 StartY=-24.6078 StartZ=0 EndX=67 EndY=-24.6078 EndZ=0
    g1: LineSegment StartX=67 StartY=-24.6078 StartZ=0 EndX=67 EndY=20.3922 EndZ=0
    g2: LineSegment StartX=67 StartY=20.3922 StartZ=0 EndX=-53 EndY=20.3922 EndZ=0
    g3: LineSegment StartX=-53 StartY=20.3922 StartZ=0 EndX=-53 EndY=-24.6078 EndZ=0
  constraints (11):
    c: Coincident(g0,g1)
    c: Coincident(g1,g2)
    c: Coincident(g2,g3)
    c: Coincident(g3,g0)
    c: Horizontal(g0)
    c: Horizontal(g2)
    c: Vertical(g1)
    c: Vertical(g3)
    c: Distance(g2) = 120
    c: DistanceX(g2) = -53
    c: Distance(g3) = 45
FEATURE [PartDesign::Body] Body002  label="ScreenBox"
  Group = -> [Sketch029,Pad005,Sketch001,Sketch028,Pocket016,Pocket017,Sketch030,Pocket018,Chamfer001,Sketch031,Pad006,Sketch032,Pocket019,Sketch033,Pocket020,Sketch034,Pocket021,Sketch010,Pad007,Sketch027,Pocket022,Sketch016,Pocket023,Chamfer002,Sketch035,Sketch022,Pocket024,Chamfer005,Chamfer006,Sketch023,Pocket025,Chamfer007]
  Origin = -> Origin002
  Placement = pos=(14,6.52211,107.834) rot=(1,0,0;0.872665rad)
  Tip = -> Chamfer007
FEATURE [Sketcher::SketchObject] Sketch036
  FullyConstrained = true
  MapMode = 5
  Placement = pos=(0,-9,1.5e-14) rot=(1,0,0;1.5708rad)
  sketch-geometry (4):
    g0: LineSegment StartX=-52.5 StartY=18.5 StartZ=0 EndX=52.5 EndY=18.5 EndZ=0
    g1: LineSegment StartX=52.5 StartY=18.5 StartZ=0 EndX=52.5 EndY=-18.5 EndZ=0
    g2: LineSegment StartX=52.5 StartY=-18.5 StartZ=0 EndX=-52.5 EndY=-18.5 EndZ=0
    g3: LineSegment StartX=-52.5 StartY=-18.5 StartZ=0 EndX=-52.5 EndY=18.5 EndZ=0
  constraints (11):
    c: Coincident(g0,g1)
    c: Coincident(g1,g2)
    c: Coincident(g2,g3)
    c: Coincident(g3,g0)
    c: Horizontal(g0)
    c: Horizontal(g2)
    c: Vertical(g1)
    c: Vertical(g3)
    c: Distance(g0) = 105
    c: Symmetric(g0,g2,g-1)
    c: Distance(g1) = 37
FEATURE [Sketcher::SketchObject] Sketch037
  FullyConstrained = true
  MapMode = 5
  Placement = pos=(0,0,0) rot=(1,0,0;1.5708rad)
  Support = -> [XZ_Plane003]
  sketch-geometry (4):
    g0: LineSegment StartX=-60 StartY=22.5 StartZ=0 EndX=60 EndY=22.5 EndZ=0
    g1: LineSegment StartX=60 StartY=22.5 StartZ=0 EndX=60 EndY=-22.5 EndZ=0
    g2: LineSegment StartX=60 StartY=-22.5 StartZ=0 EndX=-60 EndY=-22.5 EndZ=0
    g3: LineSegment StartX=-60 StartY=-22.5 StartZ=0 EndX=-60 EndY=22.5 EndZ=0
  constraints (10):
    c: Coincident(g0,g1)
    c: Coincident(g1,g2)
    c: Coincident(g2,g3)
    c: Coincident(g3,g0)
    c: Horizontal(g2)
    c: Vertical(g3)
    c: Symmetric(g0,g0,g-2)
    c: Distance(g0) = 120
    c: Distance(g1) = 45
    c: Symmetric(g1,g0,g-1)
FEATURE [PartDesign::Pad] Pad008
  Direction = (1,1,1)
  Length = 3
  Length2 = 100
  Placement = pos=(0,0,0) rot=(1,0,0;1.5708rad)
  Profile = -> Sketch037
  Type = 0
FEATURE [Sketcher::SketchObject] Sketch038
  FullyConstrained = true
  MapMode = 5
  Placement = pos=(0,-3,7e-16) rot=(1,0,0;1.5708rad)
  Support = -> [Pad008]
  sketch-geometry (4):
    g0: LineSegment StartX=-56.75 StartY=20 StartZ=0 EndX=56.75 EndY=20 EndZ=0
    g1: LineSegment StartX=56.75 StartY=20 StartZ=0 EndX=56.75 EndY=-20 EndZ=0
    g2: LineSegment StartX=56.75 StartY=-20 StartZ=0 EndX=-56.75 EndY=-20 EndZ=0
    g3: LineSegment StartX=-56.75 StartY=-20 StartZ=0 EndX=-56.75 EndY=20 EndZ=0
  constraints (11):
    c: Coincident(g0,g1)
    c: Coincident(g1,g2)
    c: Coincident(g2,g3)
    c: Coincident(g3,g0)
    c: Horizontal(g0)
    c: Horizontal(g2)
    c: Vertical(g1)
    c: Vertical(g3)
    c: Distance(g0) = 113.5
    c: Distance(g1) = 40
    c: Symmetric(g1,g0,g-1)
FEATURE [PartDesign::Pad] Pad009
  BaseFeature = -> Pad008
  Direction = (1,1,1)
  Length = 6
  Length2 = 100
  Placement = pos=(0,0,0) rot=(1,0,0;1.5708rad)
  Profile = -> Sketch038
  Type = 0
FEATURE [Sketcher::SketchObject] Sketch039
  FullyConstrained = true
  MapMode = 5
  Placement = pos=(56.75,0,0) rot=(0.707107,0,0.707107;3.14159rad)
  Support = -> [Pad009]
  sketch-geometry (1):
    g0: Circle CenterX=0 CenterY=6 CenterZ=0 NormalX=0 NormalY=0 NormalZ=1 AngleXU=0 Radius=1.4
  constraints (3):
    c: PointOnObject(g0,g-2)
    c: Diameter(g0) = 2.8
    c: DistanceY(g0) = 6
FEATURE [PartDesign::Pocket] Pocket026
  BaseFeature = -> Pad009
  Length = 5
  Length2 = 100
  Placement = pos=(0,0,0) rot=(1,0,0;1.5708rad)
  Profile = -> Sketch039
  Type = 1
FEATURE [Sketcher::SketchObject] Sketch040
  ExternalGeometry = -> [Pocket026]
  FullyConstrained = false
  MapMode = 5
  Placement = pos=(60,0,0) rot=(0.707107,0,0.707107;3.14159rad)
  Support = -> [Pocket026]
  sketch-geometry (3):
    g0: LineSegment StartX=-22.5 StartY=3 StartZ=0 EndX=-17.8755 EndY=-3.60453 EndZ=0
    g1: LineSegment StartX=-17.8755 StartY=-3.60453 StartZ=0 EndX=-35.5163 EndY=-3.60453 EndZ=0
    g2: LineSegment StartX=-35.5163 StartY=-3.60453 StartZ=0 EndX=-22.5 EndY=3 EndZ=0
  constraints (6):
    c: Coincident(g0,g1)
    c: Horizontal(g1)
    c: Coincident(g1,g2)
    c: Coincident(g2,g0)
    c: Angle(g0) = -0.959931
    c: Coincident(g0,g-3)
FEATURE [PartDesign::Pocket] Pocket027
  BaseFeature = -> Pocket026
  Length = 5
  Length2 = 100
  Placement = pos=(0,0,0) rot=(1,0,0;1.5708rad)
  Profile = -> Sketch040
  Type = 1
FEATURE [PartDesign::Mirrored] Mirrored
  BaseFeature = -> Pocket027
  MirrorPlane = -> Sketch040 [V_Axis]
  Originals = -> [Pocket027]
  Placement = pos=(0,0,0) rot=(1,0,0;1.5708rad)
FEATURE [PartDesign::Chamfer] Chamfer008
  Angle = 45
  Base = -> Mirrored [Edge14,Edge12]
  BaseFeature = -> Mirrored
  ChamferType = 0
  FlipDirection = false
  Placement = pos=(0,0,0) rot=(1,0,0;1.5708rad)
  Size = 2
  Size2 = 1
  SupportTransform = false
FEATURE [PartDesign::Pocket] Pocket028
  BaseFeature = -> Chamfer008
  Length = 6
  Length2 = 100
  Placement = pos=(0,0,0) rot=(1,0,0;1.5708rad)
  Profile = -> Sketch036
  Type = 0
FEATURE [PartDesign::Chamfer] Chamfer009
  Angle = 45
  Base = -> Pocket028 [Edge29]
  BaseFeature = -> Pocket028
  ChamferType = 0
  FlipDirection = false
  Placement = pos=(0,0,0) rot=(1,0,0;1.5708rad)
  Size = 2
  Size2 = 1
  SupportTransform = false
FEATURE [PartDesign::Chamfer] Chamfer010
  Angle = 45
  Base = -> Chamfer009 [Edge11]
  BaseFeature = -> Chamfer009
  ChamferType = 0
  FlipDirection = false
  Placement = pos=(0,0,0) rot=(1,0,0;1.5708rad)
  Size = 1
  Size2 = 1
  SupportTransform = false
FEATURE [PartDesign::Chamfer] Chamfer011
  Angle = 45
  Base = -> Chamfer010 [Edge18]
  BaseFeature = -> Chamfer010
  ChamferType = 0
  FlipDirection = false
  Placement = pos=(0,0,0) rot=(1,0,0;1.5708rad)
  Size = 1
  Size2 = 1
  SupportTransform = false
FEATURE [PartDesign::Chamfer] Chamfer012
  Angle = 45
  Base = -> Chamfer011 [Edge20]
  BaseFeature = -> Chamfer011
  ChamferType = 0
  FlipDirection = false
  Placement = pos=(0,0,0) rot=(1,0,0;1.5708rad)
  Size = 2
  Size2 = 1
  SupportTransform = false
FEATURE [PartDesign::Body] Body003  label="BoxCap"
  Group = -> [Sketch037,Pad008,Sketch038,Pad009,Sketch039,Pocket026,Sketch036,Sketch040,Pocket027,Mirrored,Chamfer008,Pocket028,Chamfer009,Chamfer010,Chamfer011,Chamfer012]
  Origin = -> Origin003
  Placement = pos=(7,30,110) rot=(0,0,1;0rad)
  Tip = -> Chamfer012
FEATURE [Sketcher::SketchObject] Sketch042  label="buttonHoles"
  FullyConstrained = false
  MapMode = 5
  Placement = pos=(40,0,0) rot=(0.57735,0.57735,0.57735;2.0944rad)
  sketch-geometry (14):
    g0: LineSegment StartX=26 StartY=10.1945 StartZ=0 EndX=33.8 EndY=14.6979 EndZ=0
    g1: LineSegment StartX=33.8 StartY=14.6979 StartZ=0 EndX=33.8 EndY=23.7045 EndZ=0
    g2: LineSegment StartX=33.8 StartY=23.7045 StartZ=0 EndX=26 EndY=28.2079 EndZ=0
    g3: LineSegment StartX=26 StartY=28.2079 StartZ=0 EndX=18.2 EndY=23.7045 EndZ=0
    g4: LineSegment StartX=18.2 StartY=23.7045 StartZ=0 EndX=18.2 EndY=14.6979 EndZ=0
    g5: LineSegment StartX=18.2 StartY=14.6979 StartZ=0 EndX=26 EndY=10.1945 EndZ=0
    g6: Circle CenterX=26 CenterY=19.2012 CenterZ=0 NormalX=0 NormalY=0 NormalZ=1 AngleXU=0 Radius=9.00666
    g7: LineSegment StartX=31.6 StartY=39.0374 StartZ=0 EndX=31.6 EndY=43.1943 EndZ=0
    g8: LineSegment StartX=31.6 StartY=43.1943 StartZ=0 EndX=28 EndY=45.2728 EndZ=0
    g9: LineSegment StartX=28 StartY=45.2728 StartZ=0 EndX=24.4 EndY=43.1943 EndZ=0
    g10: LineSegment StartX=24.4 StartY=43.1943 StartZ=0 EndX=24.4 EndY=39.0374 EndZ=0
    g11: LineSegment StartX=24.4 StartY=39.0374 StartZ=0 EndX=28 EndY=36.959 EndZ=0
    g12: LineSegment StartX=28 StartY=36.959 StartZ=0 EndX=31.6 EndY=39.0374 EndZ=0
    g13: Circle CenterX=28 CenterY=41.1159 CenterZ=0 NormalX=0 NormalY=0 NormalZ=1 AngleXU=0 Radius=4.15692
  constraints (32):
    c: Coincident(g0,g1)
    c: Coincident(g1,g2)
    c: Coincident(g2,g3)
    c: Coincident(g3,g4)
    c: Coincident(g4,g5)
    c: Coincident(g5,g0)
    c: Equal(g0, g1-g5) x5
    c: PointOnObject(g0,g6)
    c: PointOnObject(g1,g6)
    c: PointOnObject(g2,g6)
    c: PointOnObject(g3,g6)
    c: PointOnObject(g4,g6)
    c: PointOnObject(g5,g6)
    c: Coincident(g7,g8)
    c: Coincident(g8,g9)
    c: Coincident(g9,g10)
    c: Coincident(g10,g11)
    c: Coincident(g11,g12)
    c: Coincident(g12,g7)
    c: Equal(g7, g8-g12) x5
    c: PointOnObject(g7,g13)
    c: PointOnObject(g8,g13)
    c: PointOnObject(g9,g13)
    c: PointOnObject(g10,g13)
    c: PointOnObject(g11,g13)
    c: PointOnObject(g12,g13)
    c: Distance(g0,g4) = 15.6
    c: Vertical(g1)
    c: Vertical(g7)
    c: Distance(g7,g10) = 7.2
    c: DistanceX(g6) = 26
    c: DistanceX(g13) = 28
FEATURE [Sketcher::SketchObject] Sketch044  label="umbchannel"
  FullyConstrained = true
  MapMode = 5
  Placement = pos=(0,0,50) rot=(0,0,1;0rad)
  sketch-geometry (1):
    g0: Circle CenterX=-31 CenterY=23 CenterZ=0 NormalX=0 NormalY=0 NormalZ=1 AngleXU=0 Radius=5
  constraints (3):
    c: Diameter(g0) = 10
    c: DistanceX(g0) = -31
    c: DistanceY(g0) = 23
FEATURE [PartDesign::Pocket] Pocket029
  BaseFeature = -> Pad003
  Length = 5
  Length2 = 100
  Profile = -> Sketch017
  Type = 1
FEATURE [PartDesign::Pocket] Pocket030
  BaseFeature = -> Pocket029
  Length = 9
  Length2 = 100
  Profile = -> Sketch018
  Type = 0
FEATURE [PartDesign::Pocket] Pocket031
  BaseFeature = -> Pocket030
  Length = 10
  Length2 = 100
  Profile = -> Sketch019
  Type = 0
FEATURE [PartDesign::Pocket] Pocket032
  BaseFeature = -> Pocket031
  Length = 5
  Length2 = 100
  Profile = -> Sketch020
  Type = 1
FEATURE [PartDesign::Pocket] Pocket033
  BaseFeature = -> Pocket032
  Length = 5
  Length2 = 100
  Profile = -> Sketch021
  Type = 1
FEATURE [Sketcher::SketchObject] Sketch025  label="CoverBolts"
  FullyConstrained = true
  MapMode = 5
  Placement = pos=(0,40,0) rot=(0,0.707107,0.707107;3.14159rad)
  Support = -> [Pocket033]
  sketch-geometry (1):
    g0: Circle CenterX=-36 CenterY=3.5 CenterZ=0 NormalX=0 NormalY=0 NormalZ=1 AngleXU=0 Radius=2.75
  constraints (3):
    c: Diameter(g0) = 5.5
    c: DistanceY(g0) = 3.5
    c: DistanceX(g0) = -36
FEATURE [Sketcher::SketchObject] Sketch045
  FullyConstrained = true
  MapMode = 5
  Placement = pos=(0,0,0) rot=(1,0,0;1.5708rad)
  Support = -> [XZ_Plane004]
  sketch-geometry (4):
    g0: LineSegment StartX=-40 StartY=55 StartZ=0 EndX=40 EndY=55 EndZ=0
    g1: LineSegment StartX=40 StartY=55 StartZ=0 EndX=40 EndY=0 EndZ=0
    g2: LineSegment StartX=40 StartY=0 StartZ=0 EndX=-40 EndY=0 EndZ=0
    g3: LineSegment StartX=-40 StartY=0 StartZ=0 EndX=-40 EndY=55 EndZ=0
  constraints (11):
    c: Coincident(g0,g1)
    c: Coincident(g1,g2)
    c: Coincident(g2,g3)
    c: Coincident(g3,g0)
    c: Horizontal(g2)
    c: Vertical(g1)
    c: Vertical(g3)
    c: Distance(g1) = 55
    c: Distance(g0) = 80
    c: Symmetric(g0,g0,g-2)
    c: PointOnObject(g1,g-1)
FEATURE [PartDesign::Pad] Pad012
  Direction = (1,1,1)
  Length = 2
  Length2 = 100
  Placement = pos=(0,0,0) rot=(1,0,0;1.5708rad)
  Profile = -> Sketch045
  Type = 0
FEATURE [Sketcher::SketchObject] Sketch046
  FullyConstrained = true
  MapMode = 5
  Placement = pos=(0,0,0) rot=(-1,0,0;1.5708rad)
  Support = -> [Pad012]
  sketch-geometry (2):
    g0: Circle CenterX=-36 CenterY=-3.5 CenterZ=0 NormalX=0 NormalY=0 NormalZ=1 AngleXU=0 Radius=1.75
    g1: Circle CenterX=-30 CenterY=-51 CenterZ=0 NormalX=0 NormalY=0 NormalZ=1 AngleXU=0 Radius=1.75
  constraints (6):
    c: DistanceY(g1) = -51
    c: Diameter(g1) = 3.5
    c: Equal(g1,g0)
    c: DistanceX(g0) = -36
    c: DistanceX(g1) = -30
    c: DistanceY(g0) = -3.5
FEATURE [PartDesign::Pocket] Pocket037
  BaseFeature = -> Pad012
  Length = 5
  Length2 = 100
  Placement = pos=(0,0,0) rot=(1,0,0;1.5708rad)
  Profile = -> Sketch046
  Type = 0
FEATURE [PartDesign::Mirrored] Mirrored001
  BaseFeature = -> Pocket037
  MirrorPlane = -> Sketch046 [V_Axis]
  Originals = -> [Pocket037]
  Placement = pos=(0,0,0) rot=(1,0,0;1.5708rad)
FEATURE [PartDesign::Chamfer] Chamfer
  Angle = 45
  Base = -> Mirrored001 [Edge9,Edge3,Edge11,Edge6,Edge2,Edge1,Edge5,Edge8]
  BaseFeature = -> Mirrored001
  ChamferType = 0
  FlipDirection = false
  Placement = pos=(0,0,0) rot=(1,0,0;1.5708rad)
  Size = 1
  Size2 = 1
  SupportTransform = false
FEATURE [PartDesign::Body] Body004  label="Cover"
  Group = -> [Sketch045,Pad012,Sketch046,Pocket037,Mirrored001,Chamfer]
  Origin = -> Origin004
  Placement = pos=(0,42,0) rot=(0,0,1;0rad)
  Tip = -> Chamfer
FEATURE [Sketcher::SketchObject] Sketch047
  FullyConstrained = true
  MapMode = 5
  Placement = pos=(0,40,0) rot=(0,0.707107,0.707107;3.14159rad)
  sketch-geometry (4):
    g0: ArcOfCircle CenterX=-30 CenterY=1 CenterZ=0 NormalX=0 NormalY=0 NormalZ=1 AngleXU=0 Radius=3.5 StartAngle=3.14159 EndAngle=6.28319
    g1: ArcOfCircle CenterX=30 CenterY=1 CenterZ=0 NormalX=0 NormalY=0 NormalZ=1 AngleXU=0 Radius=3.5 StartAngle=3.14159 EndAngle=6.28319
    g2: LineSegment StartX=-33.5 StartY=1.00002 StartZ=0 EndX=-26.5 EndY=1.00002 EndZ=0
    g3: LineSegment StartX=26.5 StartY=1.00002 StartZ=0 EndX=33.5 EndY=1.00002 EndZ=0
  constraints (13):
    c: Coincident(g2,g0)
    c: Coincident(g2,g0)
    c: Horizontal(g2)
    c: Coincident(g3,g1)
    c: Horizontal(g3)
    c: Coincident(g3,g1)
    c: Distance(g0,g1) = 60
    c: Symmetric(g1,g0,g-2)
    c: DistanceY(g0) = 1
    c: Diameter(g0) = 7
    c: Equal(g0,g1)
    c: Equal(g2,g3)
    c: Distance(g2) = 7
FEATURE [Sketcher::SketchObject] Sketch048
  FullyConstrained = true
  MapMode = 5
  Placement = pos=(0,40,0) rot=(0,0.707107,0.707107;3.14159rad)
  sketch-geometry (2):
    g0: Circle CenterX=-30 CenterY=1 CenterZ=0 NormalX=0 NormalY=0 NormalZ=1 AngleXU=0 Radius=1.4
    g1: Circle CenterX=30 CenterY=1 CenterZ=0 NormalX=0 NormalY=0 NormalZ=1 AngleXU=0 Radius=1.4
  constraints (5):
    c: Symmetric(g1,g0,g-2)
    c: Distance(g0,g1) = 60
    c: Diameter(g1) = 2.8
    c: Equal(g1,g0)
    c: DistanceY(g0) = 1
FEATURE [PartDesign::Pad] Pad013
  BaseFeature = -> Pad001
  Direction = (1,1,1)
  Length = 6
  Length2 = 100
  Profile = -> Sketch047
  Reversed = true
  Type = 0
FEATURE [PartDesign::Pocket] Pocket038
  BaseFeature = -> Pad013
  Length = 5
  Length2 = 100
  Profile = -> Sketch048
  Type = 0
FEATURE [PartDesign::Pad] Pad014
  BaseFeature = -> Pocket033
  Direction = (1,1,1)
  Length = 6
  Length2 = 100
  Profile = -> Sketch025
  Reversed = true
  Type = 0
FEATURE [PartDesign::Mirrored] Mirrored002
  BaseFeature = -> Pad014
  MirrorPlane = -> Sketch025 [V_Axis]
  Originals = -> [Pad014]
FEATURE [Sketcher::SketchObject] Sketch049
  FullyConstrained = true
  MapMode = 5
  Placement = pos=(0,40,0) rot=(0,0.707107,0.707107;3.14159rad)
  Support = -> [Mirrored002]
  sketch-geometry (1):
    g0: Circle CenterX=-36 CenterY=3.5 CenterZ=0 NormalX=0 NormalY=0 NormalZ=1 AngleXU=0 Radius=1.4
  constraints (3):
    c: DistanceX(g0) = -36
    c: DistanceY(g0) = 3.5
    c: Diameter(g0) = 2.8
FEATURE [PartDesign::Pocket] Pocket039
  BaseFeature = -> Mirrored002
  Length = 6
  Length2 = 100
  Profile = -> Sketch049
  Type = 0
FEATURE [PartDesign::Mirrored] Mirrored003
  BaseFeature = -> Pocket039
  MirrorPlane = -> Sketch049 [V_Axis]
  Originals = -> [Pocket039]
FEATURE [PartDesign::Pocket] Pocket040
  BaseFeature = -> Mirrored003
  Length = 35
  Length2 = 100
  Profile = -> Sketch044
  Type = 0
FEATURE [PartDesign::Pad] Pad015
  BaseFeature = -> Pocket040
  Direction = (1,1,1)
  Length = 31
  Length2 = 100
  Profile = -> Sketch026
  Reversed = true
  Type = 0
FEATURE [PartDesign::Pocket] Pocket041
  BaseFeature = -> Pad015
  Length = 40
  Length2 = 100
  Profile = -> Sketch042
  Type = 0
FEATURE [PartDesign::Chamfer] Chamfer015
  Angle = 45
  Base = -> Pocket041 [Edge19,Edge11]
  BaseFeature = -> Pocket041
  ChamferType = 0
  FlipDirection = false
  Size = 1
  Size2 = 1
  SupportTransform = false
FEATURE [PartDesign::Chamfer] Chamfer016
  Angle = 45
  Base = -> Chamfer015 [Edge186,Edge199,Edge189]
  BaseFeature = -> Chamfer015
  ChamferType = 0
  FlipDirection = false
  Size = 1
  Size2 = 1
  SupportTransform = false
FEATURE [PartDesign::Chamfer] Chamfer017
  Angle = 45
  Base = -> Chamfer016 [Edge68,Edge117,Edge115,Edge78,Edge75,Edge113]
  BaseFeature = -> Chamfer016
  ChamferType = 0
  FlipDirection = false
  Size = 1
  Size2 = 1
  SupportTransform = false
FEATURE [PartDesign::Chamfer] Chamfer018
  Angle = 45
  Base = -> Chamfer017 [Edge52,Edge55,Edge47,Edge126,Edge127,Edge117]
  BaseFeature = -> Chamfer017
  ChamferType = 0
  FlipDirection = false
  Size = 1
  Size2 = 1
  SupportTransform = false
FEATURE [PartDesign::Body] Body  label="Block1"
  Group = -> [Sketch,Pad,Sketch002,Sketch004,Sketch005,Sketch006,Sketch007,Sketch008,Sketch009,Sketch013,Sketch014,Pocket,Sketch015,Pocket001,Pocket002,Pocket003,Pocket004,Pocket005,Pad002,Pocket006,Pocket007,Pad003,Sketch017,Sketch018,Sketch019,Sketch020,Sketch021,Sketch025,Sketch026,Sketch042,Sketch044,Pocket029,Pocket030,Pocket031,Pocket032,Pocket033,Pad014,Mirrored002,Sketch049,Pocket039,Mirrored003,+7 more]
  Origin = -> Origin
  Tip = -> Chamfer018
FEATURE [PartDesign::Chamfer] Chamfer019
  Angle = 45
  Base = -> Pocket038 [Edge44,Edge4,Edge7,Edge46,Edge45]
  BaseFeature = -> Pocket038
  ChamferType = 0
  FlipDirection = false
  Size = 1
  Size2 = 1
  SupportTransform = false
FEATURE [PartDesign::Chamfer] Chamfer020
  Angle = 45
  Base = -> Chamfer019 [Edge12,Edge11,Edge6]
  BaseFeature = -> Chamfer019
  ChamferType = 0
  FlipDirection = false
  Size = 1
  Size2 = 1
  SupportTransform = false
FEATURE [PartDesign::Chamfer] Chamfer021
  Angle = 45
  Base = -> Chamfer020 [Edge65]
  BaseFeature = -> Chamfer020
  ChamferType = 0
  FlipDirection = false
  Size = 1
  Size2 = 1
  SupportTransform = false
FEATURE [PartDesign::Fillet] Fillet
  Base = -> Chamfer021 [Edge20]
  BaseFeature = -> Chamfer021
  Radius = 2
  SupportTransform = false
FEATURE [PartDesign::Body] Body001  label="StepperBase"
  Group = -> [Sketch003,Pad001,Sketch047,Sketch048,Pad013,Pocket038,Chamfer019,Chamfer020,Chamfer021,Fillet]
  Origin = -> Origin001
  Placement = pos=(-6.1e-15,0,50) rot=(0,0,1;0rad)
  Tip = -> Fillet
FEATURE [Mesh::Feature] Mesh  label="Chamfer018 (Meshed)"
